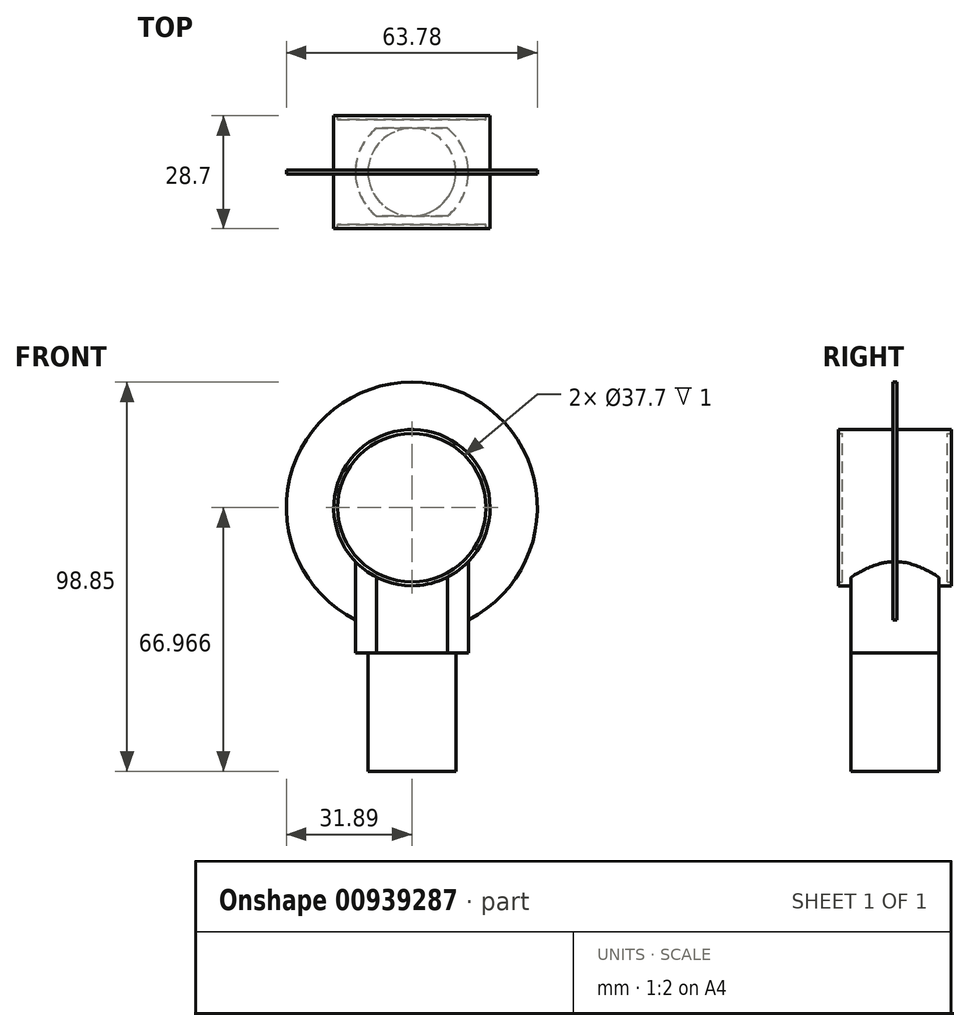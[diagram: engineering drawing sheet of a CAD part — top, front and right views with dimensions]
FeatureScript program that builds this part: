
annotation { "Feature Type Name" : "Feature", "Feature Type Description" : "" }
export const myFeature = defineFeature(function(context is Context, id is Id, definition is map)
    precondition{}
    {
        {
            var Q0;
            Q0=qCreatedBy(makeId("Top.planeOp"),FACE);
            var sketch = newSketch(context, id + "F0", { "sketchPlane" : qUnion([Q0])});
            skCircle(sketch, "E0", {"center": v(0, 0) * mm, "radius": 11.15 * mm});
            skCircle(sketch, "E1", {"center": v(0, 0) * mm, "radius": 14.35 * mm});
            skLineSegment(sketch, "E2.bottom", {"start": v(14.35, -11.15) * mm, "end": v(-14.35, -11.15) * mm});
            skLineSegment(sketch, "E2.top", {"start": v(14.35, 11.15) * mm, "end": v(-14.35, 11.15) * mm});
            skLineSegment(sketch, "E2.left", {"start": v(14.35, -11.15) * mm, "end": v(14.35, 11.15) * mm});
            skLineSegment(sketch, "E2.right", {"start": v(-14.35, -11.15) * mm, "end": v(-14.35, 11.15) * mm});
            skSolve(sketch);
        }
        {
            var Q0;
            Q0=qCreatedBy(makeId("Front.planeOp"),FACE);
            var sketch = newSketch(context, id + "F1", { "sketchPlane" : qUnion([Q0])});
            skCircle(sketch, "E3", {"center": v(0, 36.97) * mm, "radius": 18.85 * mm});
            skCircle(sketch, "E4", {"center": v(0, 36.97) * mm, "radius": 19.85 * mm});
            skCircle(sketch, "E5", {"center": v(0, 36.97) * mm, "radius": 31.89 * mm});
            skSolve(sketch);
        }
        {
            var Q0;
            Q0=makeQuery(id+"F1.imprint","IMPRINT",FACE,{"disambiguationData":[TD([[makeQuery(id+"F1.imprint","IMPRINT",EDGE,{"derivedFrom":sQuery(id+"F1.wireOp",EDGE,"E3")}),1.0]])]});
            extrude(context, id + "F2", {"entities" : qUnion([Q0]), "endBound" : BoundingType.SYMMETRIC, "depth" : 26.7 * mm, "offsetDistance" : 25 * mm});
        }
        {
            var Q0;
            Q0=makeQuery(id+"F1.imprint","IMPRINT",FACE,{"disambiguationData":[TD([[makeQuery(id+"F1.imprint","IMPRINT",EDGE,{"derivedFrom":sQuery(id+"F1.wireOp",EDGE,"E3")}),-1.0]])]});
            extrude(context, id + "F3", {"entities" : qUnion([Q0]), "operationType" : NewBodyOperationType.ADD, "endBound" : BoundingType.SYMMETRIC, "depth" : 28.7 * mm, "offsetDistance" : 25 * mm});
        }
        {
            var Q0;
            Q0=makeQuery(id+"F0.imprint","IMPRINT",FACE,{"disambiguationData":[TD([[makeQuery(id+"F0.imprint","IMPRINT",EDGE,{"derivedFrom":sQuery(id+"F0.wireOp",EDGE,"E0")}),1.0]])]});
            var Q1;
            {var subQ3=sQuery(id+"F0.wireOp",EDGE,"E0");var subQ6=sQuery(id+"F0.wireOp",EDGE,"E2.top");var subQ8=makeQuery(id+"F0.imprint","INTERSECT",VERTEX,{"disambiguationData":[OD(1.0)],"derivedFrom":[subQ3,subQ6]});Q1=makeQuery(id+"F0.imprint","IMPRINT",FACE,{"disambiguationData":[TD([[makeQuery(id+"F0.imprint","IMPRINT",EDGE,{"disambiguationData":[TD([[subQ8,1.0]])],"derivedFrom":subQ3}),-1.0]])]});}
            var Q2;
            {var subQ3=sQuery(id+"F0.wireOp",EDGE,"E0");var subQ6=sQuery(id+"F0.wireOp",EDGE,"E2.top");var subQ8=makeQuery(id+"F0.imprint","INTERSECT",VERTEX,{"disambiguationData":[OD(0.0)],"derivedFrom":[subQ3,subQ6]});Q2=makeQuery(id+"F0.imprint","IMPRINT",FACE,{"disambiguationData":[TD([[makeQuery(id+"F0.imprint","IMPRINT",EDGE,{"disambiguationData":[TD([[subQ8,-1.0]])],"derivedFrom":subQ3}),-1.0]])]});}
            extrude(context, id + "F4", {"entities" : qUnion([Q0, Q1, Q2]), "depth" : 34.2 * mm, "offsetDistance" : 25 * mm});
        }
        {
            var Q0;
            Q0=makeQuery(id+"F0.imprint","IMPRINT",FACE,{"disambiguationData":[TD([[makeQuery(id+"F0.imprint","IMPRINT",EDGE,{"derivedFrom":sQuery(id+"F0.wireOp",EDGE,"E0")}),1.0]])]});
            extrude(context, id + "F5", {"entities" : qUnion([Q0]), "operationType" : NewBodyOperationType.ADD, "oppositeDirection" : true, "depth" : 30 * mm, "offsetDistance" : 25 * mm});
        }
        {
            var Q0;
            Q0=makeQuery(id+"F1.imprint","IMPRINT",FACE,{"disambiguationData":[TD([[makeQuery(id+"F1.imprint","IMPRINT",EDGE,{"derivedFrom":sQuery(id+"F1.wireOp",EDGE,"E3")}),-1.0]])]});
            var Q1;
            Q1=makeQuery(id+"F1.imprint","IMPRINT",FACE,{"disambiguationData":[TD([[makeQuery(id+"F1.imprint","IMPRINT",EDGE,{"derivedFrom":sQuery(id+"F1.wireOp",EDGE,"E3")}),1.0]])]});
            extrude(context, id + "F6", {"entities" : qUnion([Q0, Q1]), "endBound" : BoundingType.SYMMETRIC, "depth" : 41.8 * mm, "offsetDistance" : 25 * mm});
        }
        {
            var Q0;
            Q0=makeQuery(id+"F6.opExtrude","SWEPT_BODY",BODY,{"disambiguationData":[OSD([sQuery(id+"F1.wireOp",EDGE,"E4")])]});
            var Q1;
            Q1=makeQuery(id+"F4.opExtrude","SWEPT_BODY",BODY,{"disambiguationData":[OSD([sQuery(id+"F0.wireOp",EDGE,"E1")])]});
            booleanBodies(context, id + "F7", {"operationType" : BooleanOperationType.SUBTRACTION, "tools" : qUnion([Q0]), "targets" : qUnion([Q1])});
        }
        {
            var Q0;
            Q0=makeQuery(id+"F1.imprint","IMPRINT",FACE,{"disambiguationData":[TD([[makeQuery(id+"F1.imprint","IMPRINT",EDGE,{"derivedFrom":sQuery(id+"F1.wireOp",EDGE,"E4")}),-1.0]])]});
            extrude(context, id + "F8", {"entities" : qUnion([Q0]), "operationType" : NewBodyOperationType.ADD, "endBound" : BoundingType.SYMMETRIC, "depth" : 1 * mm, "offsetDistance" : 25 * mm});
        }
    });
